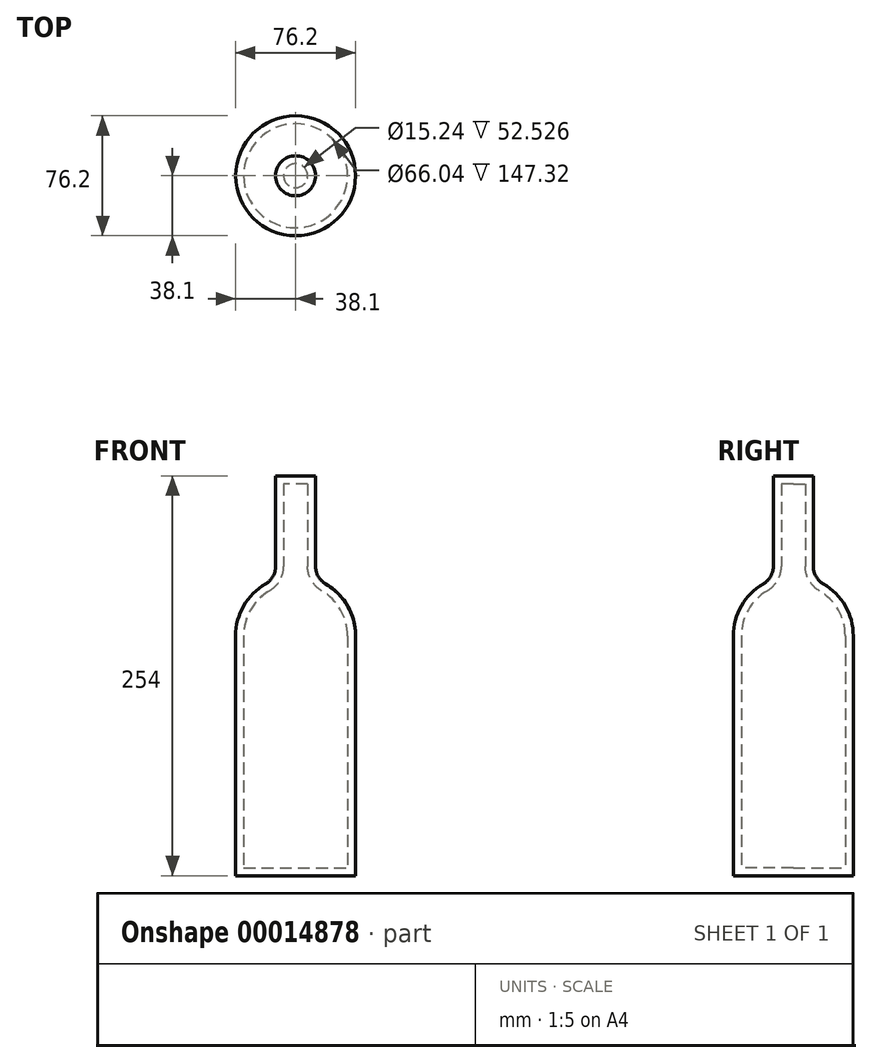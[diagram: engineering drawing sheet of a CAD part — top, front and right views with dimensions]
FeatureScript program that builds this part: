
annotation { "Feature Type Name" : "Feature", "Feature Type Description" : "" }
export const myFeature = defineFeature(function(context is Context, id is Id, definition is map)
    precondition{}
    {
        {
            var Q0;
            Q0=qCreatedBy(makeId("Top.planeOp"),FACE);
            var sketch = newSketch(context, id + "F0", { "sketchPlane" : qUnion([Q0])});
            skCircle(sketch, "E0", {"center": v(0, 0) * mm, "radius": 38.1 * mm});
            skCircle(sketch, "E1", {"center": v(0, 0) * mm, "radius": 12.7 * mm});
            skSolve(sketch);
        }
        {
            var Q0;
            Q0=makeQuery(id+"F0.imprint","IMPRINT",FACE,{"disambiguationData":[TD([[makeQuery(id+"F0.imprint","IMPRINT",EDGE,{"derivedFrom":sQuery(id+"F0.wireOp",EDGE,"E0")}),1.0]])]});
            extrude(context, id + "F1", {"entities" : qUnion([Q0]), "depth" : 152.4 * mm});
        }
        {
            var Q0;
            Q0=qCreatedBy(makeId("Front.planeOp"),FACE);
            var sketch = newSketch(context, id + "F2", { "sketchPlane" : qUnion([Q0])});
            skLineSegment(sketch, "E2", {"start": v(0, 152.4) * mm, "end": v(-38.1, 152.4) * mm});
            skArc(sketch, "E3", {"start": v(0, 190.5) * mm, "mid": v(-26.94, 179.34) * mm, "end": v(-38.1, 152.4) * mm});
            skLineSegment(sketch, "E4", {"start": v(0, 152.4) * mm, "end": v(0, 190.5) * mm});
            skSolve(sketch);
        }
        {
            var Q0;
            Q0=makeQuery(id+"F2.imprint","IMPRINT",FACE,{"disambiguationData":[TD([[makeQuery(id+"F2.imprint","IMPRINT",EDGE,{"derivedFrom":sQuery(id+"F2.wireOp",EDGE,"E2")}),-1.0]])]});
            var Q1;
            Q1=sQuery(id+"F2.wireOp",EDGE,"E4");
            revolve(context, id + "F3", {"operationType" : NewBodyOperationType.ADD, "entities" : qUnion([Q0]), "axis" : qUnion([Q1]), "revolveType" : RevolveType.FULL});
        }
        {
            var Q0;
            Q0=makeQuery(id+"F0.imprint","IMPRINT",FACE,{"disambiguationData":[TD([[makeQuery(id+"F0.imprint","IMPRINT",EDGE,{"derivedFrom":sQuery(id+"F0.wireOp",EDGE,"E1")}),1.0]])]});
            extrude(context, id + "F4", {"entities" : qUnion([Q0]), "operationType" : NewBodyOperationType.ADD, "depth" : 254 * mm});
        }
        {
            var Q0;
            Q0=makeQuery(id+"F4.boolean.opBoolean","INTERSECT",EDGE,{"derivedFrom":[makeQuery(id+"F3.opRevolve","SWEPT_FACE",FACE,{"disambiguationData":[OSD([sQuery(id+"F2.wireOp",EDGE,"E3")])]}),makeQuery(id+"F4.opExtrude","SWEPT_FACE",FACE,{"disambiguationData":[OSD([sQuery(id+"F0.wireOp",EDGE,"E1")])]})]});
            fillet(context, id + "F5", {"entities" : qUnion([Q0]), "radius" : 12.7 * mm, "tangentPropagation" : true, "allowEdgeOverflow" : false});
        }
        {
            var Q0;
            Q0=makeQuery(id+"F1.opExtrude","SWEPT_FACE",FACE,{"disambiguationData":[OSD([sQuery(id+"F0.wireOp",EDGE,"E0")])]});
            var Q1;
            Q1=makeQuery(id+"F3.opRevolve","SWEPT_FACE",FACE,{"disambiguationData":[OSD([sQuery(id+"F2.wireOp",EDGE,"E3")])]});
            var Q2;
            Q2=makeQuery(id+"F5.opFillet","BLEND_FACE",FACE,{"disambiguationData":[OSD([sQuery(id+"F0.wireOp",EDGE,"E1"),sQuery(id+"F2.wireOp",EDGE,"E3")])]});
            var Q3;
            Q3=makeQuery(id+"F4.opExtrude","SWEPT_FACE",FACE,{"disambiguationData":[OSD([sQuery(id+"F0.wireOp",EDGE,"E1")])]});
            var Q4;
            Q4=makeQuery(id+"F1.opExtrude","SWEPT_BODY",BODY,{"disambiguationData":[OSD([sQuery(id+"F0.wireOp",EDGE,"E0"),sQuery(id+"F0.wireOp",EDGE,"E1")])]});
            shell(context, id + "F6", {"isHollow" : true, "entities" : qUnion([Q0, Q1, Q2, Q3]), "parts" : qUnion([Q4]), "thickness" : 5.08 * mm});
        }
    });
